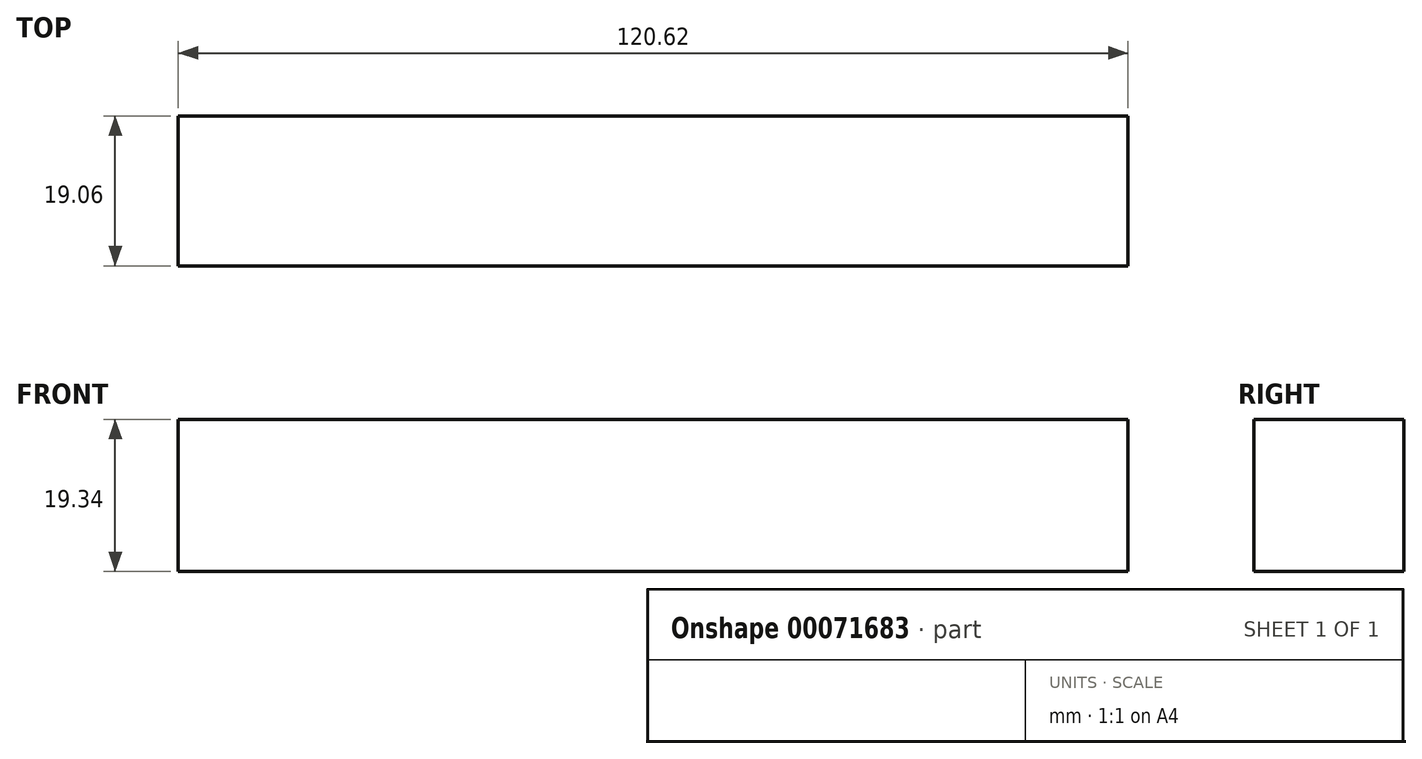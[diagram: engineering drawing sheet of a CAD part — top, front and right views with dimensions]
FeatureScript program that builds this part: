
annotation { "Feature Type Name" : "Feature", "Feature Type Description" : "" }
export const myFeature = defineFeature(function(context is Context, id is Id, definition is map)
    precondition{}
    {
        {
            var Q0;
            Q0=qCreatedBy(makeId("Front.planeOp"),FACE);
            var sketch = newSketch(context, id + "F0", { "sketchPlane" : qUnion([Q0])});
            skLineSegment(sketch, "E0.rect.bottom", {"start": v(60.31, -9.67) * mm, "end": v(-60.31, -9.67) * mm});
            skLineSegment(sketch, "E0.rect.top", {"start": v(60.31, 9.67) * mm, "end": v(-60.31, 9.67) * mm});
            skLineSegment(sketch, "E0.rect.left", {"start": v(60.31, -9.67) * mm, "end": v(60.31, 9.67) * mm});
            skLineSegment(sketch, "E0.rect.right", {"start": v(-60.31, -9.67) * mm, "end": v(-60.31, 9.67) * mm});
            skPoint(sketch, "E0.rect.middle", {"position": v(0, 0) * mm});
            skSolve(sketch);
        }
        {
            var Q0;
            Q0=makeQuery(id+"F0.imprint","IMPRINT",FACE,{"disambiguationData":[TD([[makeQuery(id+"F0.imprint","IMPRINT",EDGE,{"derivedFrom":sQuery(id+"F0.wireOp",EDGE,"E0.rect.bottom")}),-1.0]])]});
            extrude(context, id + "F1", {"entities" : qUnion([Q0]), "endBound" : BoundingType.SYMMETRIC, "depth" : 19.05 * mm});
        }
    });
